# Revit family: REVIT-TPL-2017
name_source: partatom
category: Mechanical Equipment
revit_build: Autodesk Revit 2017 (Build: 20190507_1515(x64)
units: mm (PartAtom-declared; Revit-internal decimal feet)

## family parameters
Always vertical = No
Cut with Voids When Loaded = No
Part Type = Normal
Room Calculation Point = No
Round Connector Dimension = Use Radius
Shared = No
Work Plane-Based = No

## types (21) — shared parameters
Air Inlet Diameter = 6"
Air Inlet Extension = 18"
Air Inlet Radius = 3"
Apparent Load = 120 VA
Assembly Code = D3040400
Description = PVI Turbopower Low NOx- Water Heater
Disclaimer = This rendering is for building modeling purposes only. Submittal/catalog is still the contract document. PVI reserves the right to change design and specification without notice.
Drain Angle = 0.00°
Enclosure Location = 4"
Energy Radius = 14 1/2"
Flue Collector Radius = 11 1/4"
Flue Diameter = 8"
Flue Extension = 18 1/4"
Flue Radius = 4"
Gas Inlet Extension = 22"
Manufacturer = PVI Industries, LLC
NOx Extension = 18"
NOx Radius = 17"
Rear Access Extension = 0"
Relief Valve NPT = 1"
Relief Valve Radius = 1/2"
URL = www.pvi.com

## per-type parameters (varying)
- 1000 X 150A-TPL: Air Inlet Location=54 3/8"; Cold Water Extension=19 1/8"; Cold Water NPT=2"; Cold Water Radius=1"; Control Panel Extension=25 1/8"; Current=9 A; Drain Extension=21 1/8"; Drain NPT=1"; Drain Radius=1/2"; Energy Extension=37 1/8"; FC OAL=45 3/8"; Flat Side Distance=34"; Flue Collector Extension=8 1/4"; Flue Location=41 1/4"; Front Skid Extension=54 3/8"; Gas Inlet Height=32 1/2"; Gas Inlet NPT=1"; Gas Inlet Radius=1/2"; Height to Cold Inlet=17"; Height to Drain=1 7/8"; Height to Energy=26 1/2"; Height to Hot Outlet=44 7/8"; Height to Relief=51 7/8"; Hot Outlet Angle=0.00°; Hot Water Extension=19 1/8"; Hot Water NPT=2"; Hot Water Radius=1"; Input Btu/h=800000; Rear Skid Extension=18 1/8"; Recovery Rate 40F to 140F (gph)=800; Relief Extension=22 1/8"; Skid Center Dist=8 1/2"; Skid Length=36 1/4"; Skid Spacing=17"; Unit Height=63"; Unit Radius=18 1/8"; Weight=1325
- 1000 X 175A-TPL: Air Inlet Location=54 3/8"; Cold Water Extension=19 1/8"; Cold Water NPT=2"; Cold Water Radius=1"; Control Panel Extension=25 1/8"; Current=9 A; Drain Extension=21 1/8"; Drain NPT=1"; Drain Radius=1/2"; Energy Extension=37 1/8"; FC OAL=45 3/8"; Flat Side Distance=34"; Flue Collector Extension=8 1/4"; Flue Location=41 1/4"; Front Skid Extension=54 3/8"; Gas Inlet Height=32 1/2"; Gas Inlet NPT=1"; Gas Inlet Radius=1/2"; Height to Cold Inlet=17"; Height to Drain=1 7/8"; Height to Energy=26 1/2"; Height to Hot Outlet=50 7/8"; Height to Relief=57 7/8"; Hot Outlet Angle=0.00°; Hot Water Extension=19 1/8"; Hot Water NPT=2"; Hot Water Radius=1"; Input Btu/h=800000; Rear Skid Extension=18 1/8"; Recovery Rate 40F to 140F (gph)=800; Relief Extension=22 1/8"; Skid Center Dist=8 1/2"; Skid Length=36 1/4"; Skid Spacing=17"; Unit Height=69"; Unit Radius=18 1/8"; Weight=1380
- 1000 X 215A-TPL: Air Inlet Location=54 3/8"; Cold Water Extension=19 1/8"; Cold Water NPT=2"; Cold Water Radius=1"; Control Panel Extension=25 1/8"; Current=9 A; Drain Extension=21 1/8"; Drain NPT=1"; Drain Radius=1/2"; Energy Extension=37 1/8"; FC OAL=45 3/8"; Flat Side Distance=34"; Flue Collector Extension=8 1/4"; Flue Location=41 1/4"; Front Skid Extension=54 3/8"; Gas Inlet Height=32 1/2"; Gas Inlet NPT=1"; Gas Inlet Radius=1/2"; Height to Cold Inlet=17"; Height to Drain=1 7/8"; Height to Energy=26 1/2"; Height to Hot Outlet=64 1/4"; Height to Relief=64 7/8"; Hot Outlet Angle=90.00°; Hot Water Extension=19 1/8"; Hot Water NPT=2"; Hot Water Radius=1"; Input Btu/h=800000; Rear Skid Extension=18 1/8"; Recovery Rate 40F to 140F (gph)=800; Relief Extension=22 1/8"; Skid Center Dist=8 1/2"; Skid Length=36 1/4"; Skid Spacing=17"; Unit Height=76"; Unit Radius=18 1/8"; Weight=1430
- 1000 X 250A-TPL: Air Inlet Location=44 3/8"; Cold Water Extension=23 5/8"; Cold Water NPT=2"; Cold Water Radius=1"; Control Panel Extension=29 5/8"; Current=9 A; Drain Extension=25 5/8"; Drain NPT=1"; Drain Radius=1/2"; Energy Extension=27 1/8"; FC OAL=35 3/8"; Flat Side Distance=45 1/4"; Flue Collector Extension=8 1/4"; Flue Location=31 1/4"; Front Skid Extension=68 1/8"; Gas Inlet Height=32 1/2"; Gas Inlet NPT=1 1/4"; Gas Inlet Radius=5/8"; Height to Cold Inlet=17"; Height to Drain=1 7/8"; Height to Energy=28 3/4"; Height to Hot Outlet=38 7/8"; Height to Relief=45 1/8"; Hot Outlet Angle=0.00°; Hot Water Extension=23 5/8"; Hot Water NPT=2"; Hot Water Radius=1"; Input Btu/h=800000; Rear Skid Extension=22 5/8"; Recovery Rate 40F to 140F (gph)=800; Relief Extension=26 5/8"; Skid Center Dist=13 1/2"; Skid Length=45 1/2"; Skid Spacing=27"; Unit Height=61 1/2"; Unit Radius=22 5/8"; Weight=1380
- 1500 X 250A-TPL: Air Inlet Location=62 5/8"; Cold Water Extension=23 5/8"; Cold Water NPT=2"; Cold Water Radius=1"; Control Panel Extension=29 5/8"; Current=16 A; Drain Extension=25 5/8"; Drain NPT=1"; Drain Radius=1/2"; Energy Extension=38 1/8"; FC OAL=53 5/8"; Flat Side Distance=45 1/4"; Flue Collector Extension=15 1/2"; Flue Location=45 7/8"; Front Skid Extension=77 5/8"; Gas Inlet Height=32 1/2"; Gas Inlet NPT=2"; Gas Inlet Radius=1"; Height to Cold Inlet=17"; Height to Drain=1 7/8"; Height to Energy=28 3/4"; Height to Hot Outlet=38 7/8"; Height to Relief=45 1/8"; Hot Outlet Angle=0.00°; Hot Water Extension=23 5/8"; Hot Water NPT=2"; Hot Water Radius=1"; Input Btu/h=1200000; Rear Skid Extension=22 5/8"; Recovery Rate 40F to 140F (gph)=1200; Relief Extension=26 5/8"; Skid Center Dist=13 1/2"; Skid Length=55"; Skid Spacing=27"; Unit Height=61 1/2"; Unit Radius=22 5/8"; Weight=1750
- 1000 X 300A-TPL: Air Inlet Location=44 3/8"; Cold Water Extension=23 5/8"; Cold Water NPT=2"; Cold Water Radius=1"; Control Panel Extension=29 5/8"; Current=9 A; Drain Extension=25 5/8"; Drain NPT=1"; Drain Radius=1/2"; Energy Extension=27 1/8"; FC OAL=35 3/8"; Flat Side Distance=45 1/4"; Flue Collector Extension=8 1/4"; Flue Location=31 1/4"; Front Skid Extension=68 1/8"; Gas Inlet Height=32 1/2"; Gas Inlet NPT=1 1/4"; Gas Inlet Radius=5/8"; Height to Cold Inlet=17"; Height to Drain=1 7/8"; Height to Energy=28 3/4"; Height to Hot Outlet=50 7/8"; Height to Relief=57 1/8"; Hot Outlet Angle=0.00°; Hot Water Extension=23 5/8"; Hot Water NPT=2"; Hot Water Radius=1"; Input Btu/h=800000; Rear Skid Extension=22 5/8"; Recovery Rate 40F to 140F (gph)=800; Relief Extension=26 5/8"; Skid Center Dist=13 1/2"; Skid Length=45 1/2"; Skid Spacing=27"; Unit Height=73 1/2"; Unit Radius=22 5/8"; Weight=1445
- 1500 X 300A-TPL: Air Inlet Location=62 5/8"; Cold Water Extension=23 5/8"; Cold Water NPT=2"; Cold Water Radius=1"; Control Panel Extension=29 5/8"; Current=16 A; Drain Extension=25 5/8"; Drain NPT=1"; Drain Radius=1/2"; Energy Extension=38 1/8"; FC OAL=53 5/8"; Flat Side Distance=45 1/4"; Flue Collector Extension=15 1/2"; Flue Location=45 7/8"; Front Skid Extension=77 5/8"; Gas Inlet Height=32 1/2"; Gas Inlet NPT=2"; Gas Inlet Radius=1"; Height to Cold Inlet=17"; Height to Drain=1 7/8"; Height to Energy=28 3/4"; Height to Hot Outlet=50 7/8"; Height to Relief=57 1/8"; Hot Outlet Angle=0.00°; Hot Water Extension=23 5/8"; Hot Water NPT=2"; Hot Water Radius=1"; Input Btu/h=1200000; Rear Skid Extension=22 5/8"; Recovery Rate 40F to 140F (gph)=1200; Relief Extension=26 5/8"; Skid Center Dist=13 1/2"; Skid Length=55"; Skid Spacing=27"; Unit Height=73 1/2"; Unit Radius=22 5/8"; Weight=1840
- 1000 X 400A-TPL: Air Inlet Location=44 3/8"; Cold Water Extension=23 5/8"; Cold Water NPT=2"; Cold Water Radius=1"; Control Panel Extension=29 5/8"; Current=9 A; Drain Extension=25 5/8"; Drain NPT=1"; Drain Radius=1/2"; Energy Extension=27 1/8"; FC OAL=35 3/8"; Flat Side Distance=45 1/4"; Flue Collector Extension=8 1/4"; Flue Location=31 1/4"; Front Skid Extension=68 1/8"; Gas Inlet Height=32 1/2"; Gas Inlet NPT=1"; Gas Inlet Radius=1/2"; Height to Cold Inlet=17"; Height to Drain=1 7/8"; Height to Energy=28 3/4"; Height to Hot Outlet=68 1/2"; Height to Relief=69 1/8"; Hot Outlet Angle=90.00°; Hot Water Extension=23 5/8"; Hot Water NPT=2"; Hot Water Radius=1"; Input Btu/h=800000; Rear Skid Extension=22 5/8"; Recovery Rate 40F to 140F (gph)=800; Relief Extension=26 5/8"; Skid Center Dist=13 1/2"; Skid Length=45 1/2"; Skid Spacing=27"; Unit Height=85 1/2"; Unit Radius=22 5/8"; Weight=1575
- 1500 X 400A-TPL: Air Inlet Location=62 5/8"; Cold Water Extension=23 5/8"; Cold Water NPT=2"; Cold Water Radius=1"; Control Panel Extension=29 5/8"; Current=16 A; Drain Extension=25 5/8"; Drain NPT=1"; Drain Radius=1/2"; Energy Extension=38 1/8"; FC OAL=53 5/8"; Flat Side Distance=45 1/4"; Flue Collector Extension=15 1/2"; Flue Location=45 7/8"; Front Skid Extension=77 5/8"; Gas Inlet Height=32 1/2"; Gas Inlet NPT=1 1/4"; Gas Inlet Radius=5/8"; Height to Cold Inlet=17"; Height to Drain=1 7/8"; Height to Energy=28 3/4"; Height to Hot Outlet=68 1/2"; Height to Relief=69 1/8"; Hot Outlet Angle=90.00°; Hot Water Extension=23 5/8"; Hot Water NPT=2"; Hot Water Radius=1"; Input Btu/h=1200000; Rear Skid Extension=22 5/8"; Recovery Rate 40F to 140F (gph)=1200; Relief Extension=26 5/8"; Skid Center Dist=13 1/2"; Skid Length=55"; Skid Spacing=27"; Unit Height=85 1/2"; Unit Radius=22 5/8"; Weight=1925
- 1000 X 500 A-TPL: Air Inlet Location=49 7/8"; Cold Water Extension=28 7/8"; Cold Water NPT=3"; Cold Water Radius=1 1/2"; Control Panel Extension=34 7/8"; Current=9 A; Drain Extension=30 7/8"; Drain NPT=1 1/2"; Drain Radius=3/4"; Energy Extension=32 5/8"; FC OAL=40 7/8"; Flat Side Distance=55 3/4"; Flue Collector Extension=8 1/4"; Flue Location=36 3/4"; Front Skid Extension=82 7/8"; Gas Inlet Height=33 1/2"; Gas Inlet NPT=1"; Gas Inlet Radius=1/2"; Height to Cold Inlet=18 1/4"; Height to Drain=2 1/4"; Height to Energy=30"; Height to Hot Outlet=57 3/8"; Height to Relief=58"; Hot Outlet Angle=90.00°; Hot Water Extension=28 7/8"; Hot Water NPT=3"; Hot Water Radius=1 1/2"; Input Btu/h=800000; Rear Skid Extension=27 7/8"; Recovery Rate 40F to 140F (gph)=800; Relief Extension=31 7/8"; Skid Center Dist=13 1/2"; Skid Length=55"; Skid Spacing=27"; Unit Height=75 3/4"; Unit Radius=27 7/8"; Weight=2100
- 1000 X 600 A-TPL: Air Inlet Location=49 7/8"; Cold Water Extension=28 7/8"; Cold Water NPT=3"; Cold Water Radius=1 1/2"; Control Panel Extension=34 7/8"; Current=9 A; Drain Extension=30 7/8"; Drain NPT=1 1/2"; Drain Radius=3/4"; Energy Extension=32 5/8"; FC OAL=40 7/8"; Flat Side Distance=55 3/4"; Flue Collector Extension=8 1/4"; Flue Location=36 3/4"; Front Skid Extension=82 7/8"; Gas Inlet Height=33 1/2"; Gas Inlet NPT=1"; Gas Inlet Radius=1/2"; Height to Cold Inlet=18 1/4"; Height to Drain=2 1/4"; Height to Energy=30"; Height to Hot Outlet=69 3/8"; Height to Relief=70"; Hot Outlet Angle=90.00°; Hot Water Extension=28 7/8"; Hot Water NPT=3"; Hot Water Radius=1 1/2"; Input Btu/h=800000; Rear Skid Extension=27 7/8"; Recovery Rate 40F to 140F (gph)=800; Relief Extension=31 7/8"; Skid Center Dist=13 1/2"; Skid Length=55"; Skid Spacing=27"; Unit Height=87 3/4"; Unit Radius=27 7/8"; Weight=2180
- 1500 X 500 A-TPL: Air Inlet Location=57 7/8"; Cold Water Extension=28 7/8"; Cold Water NPT=3"; Cold Water Radius=1 1/2"; Control Panel Extension=34 7/8"; Current=16 A; Drain Extension=30 7/8"; Drain NPT=1 1/2"; Drain Radius=3/4"; Energy Extension=33 3/8"; FC OAL=48 7/8"; Flat Side Distance=55 3/4"; Flue Collector Extension=15 1/2"; Flue Location=41 1/8"; Front Skid Extension=82 7/8"; Gas Inlet Height=33 1/2"; Gas Inlet NPT=1 1/4"; Gas Inlet Radius=5/8"; Height to Cold Inlet=18 1/4"; Height to Drain=2 1/4"; Height to Energy=30"; Height to Hot Outlet=57 3/8"; Height to Relief=70"; Hot Outlet Angle=90.00°; Hot Water Extension=28 7/8"; Hot Water NPT=3"; Hot Water Radius=1 1/2"; Input Btu/h=1200000; Rear Skid Extension=27 7/8"; Recovery Rate 40F to 140F (gph)=1200; Relief Extension=31 7/8"; Skid Center Dist=13 1/2"; Skid Length=55"; Skid Spacing=27"; Unit Height=75 3/4"; Unit Radius=27 7/8"; Weight=2370
- 1500 X 600 A-TPL: Air Inlet Location=57 7/8"; Cold Water Extension=28 7/8"; Cold Water NPT=3"; Cold Water Radius=1 1/2"; Control Panel Extension=34 7/8"; Current=16 A; Drain Extension=30 7/8"; Drain NPT=1 1/2"; Drain Radius=3/4"; Energy Extension=33 3/8"; FC OAL=48 7/8"; Flat Side Distance=55 3/4"; Flue Collector Extension=15 1/2"; Flue Location=41 1/8"; Front Skid Extension=82 7/8"; Gas Inlet Height=33 1/2"; Gas Inlet NPT=1 1/4"; Gas Inlet Radius=5/8"; Height to Cold Inlet=18 1/4"; Height to Drain=2 1/4"; Height to Energy=30"; Height to Hot Outlet=69 3/8"; Height to Relief=58"; Hot Outlet Angle=90.00°; Hot Water Extension=28 7/8"; Hot Water NPT=3"; Hot Water Radius=1 1/2"; Input Btu/h=1200000; Rear Skid Extension=27 7/8"; Recovery Rate 40F to 140F (gph)=1200; Relief Extension=31 7/8"; Skid Center Dist=13 1/2"; Skid Length=55"; Skid Spacing=27"; Unit Height=87 3/4"; Unit Radius=27 7/8"; Weight=2445
- 1000 X 750 A-TPL: Air Inlet Location=55 1/2"; Cold Water Extension=34 1/4"; Cold Water NPT=3"; Cold Water Radius=1 1/2"; Control Panel Extension=40 1/4"; Current=9 A; Drain Extension=36 1/4"; Drain NPT=1 1/2"; Drain Radius=3/4"; Energy Extension=38 1/4"; FC OAL=46 1/2"; Flat Side Distance=66 1/2"; Flue Collector Extension=8 1/4"; Flue Location=42 3/8"; Front Skid Extension=100 1/4"; Gas Inlet Height=36 1/2"; Gas Inlet NPT=1"; Gas Inlet Radius=1/2"; Height to Cold Inlet=21 1/4"; Height to Drain=2 1/4"; Height to Energy=32 5/8"; Height to Hot Outlet=60 7/8"; Height to Relief=61 1/2"; Hot Outlet Angle=90.00°; Hot Water Extension=34 1/4"; Hot Water NPT=3"; Hot Water Radius=1 1/2"; Input Btu/h=800000; Rear Skid Extension=33 1/4"; Recovery Rate 40F to 140F (gph)=800; Relief Extension=37 1/4"; Skid Center Dist=18"; Skid Length=67"; Skid Spacing=36"; Unit Height=81 1/4"; Unit Radius=33 1/4"; Weight=2280
- 1500 X 750 A-TPL: Air Inlet Location=63 1/2"; Cold Water Extension=34 1/4"; Cold Water NPT=3"; Cold Water Radius=1 1/2"; Control Panel Extension=40 1/4"; Current=16 A; Drain Extension=36 1/4"; Drain NPT=1 1/2"; Drain Radius=3/4"; Energy Extension=39"; FC OAL=54 1/2"; Flat Side Distance=66 1/2"; Flue Collector Extension=15 1/2"; Flue Location=46 3/4"; Front Skid Extension=100 1/4"; Gas Inlet Height=36 1/2"; Gas Inlet NPT=1 1/4"; Gas Inlet Radius=5/8"; Height to Cold Inlet=21 1/4"; Height to Drain=2 1/4"; Height to Energy=32 5/8"; Height to Hot Outlet=60 7/8"; Height to Relief=61 1/2"; Hot Outlet Angle=90.00°; Hot Water Extension=34 1/4"; Hot Water NPT=3"; Hot Water Radius=1 1/2"; Input Btu/h=1200000; Rear Skid Extension=33 1/4"; Recovery Rate 40F to 140F (gph)=1200; Relief Extension=37 1/4"; Skid Center Dist=18"; Skid Length=67"; Skid Spacing=36"; Unit Height=81 1/4"; Unit Radius=33 1/4"; Weight=2320
- 1000 X 900 A-TPL: Air Inlet Location=55 1/2"; Cold Water Extension=34 1/4"; Cold Water NPT=3"; Cold Water Radius=1 1/2"; Control Panel Extension=40 1/4"; Current=9 A; Drain Extension=36 1/4"; Drain NPT=1 1/2"; Drain Radius=3/4"; Energy Extension=38 1/4"; FC OAL=46 1/2"; Flat Side Distance=66 1/2"; Flue Collector Extension=8 1/4"; Flue Location=42 3/8"; Front Skid Extension=100 1/4"; Gas Inlet Height=36 1/2"; Gas Inlet NPT=1"; Gas Inlet Radius=1/2"; Height to Cold Inlet=21 1/4"; Height to Drain=2 1/4"; Height to Energy=32 5/8"; Height to Hot Outlet=72 7/8"; Height to Relief=73 1/2"; Hot Outlet Angle=90.00°; Hot Water Extension=34 1/4"; Hot Water NPT=3"; Hot Water Radius=1 1/2"; Input Btu/h=800000; Rear Skid Extension=33 1/4"; Recovery Rate 40F to 140F (gph)=800; Relief Extension=37 1/4"; Skid Center Dist=18"; Skid Length=67"; Skid Spacing=36"; Unit Height=93 1/4"; Unit Radius=33 1/4"; Weight=2550
- 1500 X 900 A-TPL: Air Inlet Location=63 1/2"; Cold Water Extension=34 1/4"; Cold Water NPT=3"; Cold Water Radius=1 1/2"; Control Panel Extension=40 1/4"; Current=16 A; Drain Extension=36 1/4"; Drain NPT=1 1/2"; Drain Radius=3/4"; Energy Extension=39"; FC OAL=54 1/2"; Flat Side Distance=66 1/2"; Flue Collector Extension=15 1/2"; Flue Location=46 3/4"; Front Skid Extension=100 1/4"; Gas Inlet Height=36 1/2"; Gas Inlet NPT=1 1/4"; Gas Inlet Radius=5/8"; Height to Cold Inlet=21 1/4"; Height to Drain=2 1/4"; Height to Energy=32 5/8"; Height to Hot Outlet=72 7/8"; Height to Relief=73 1/2"; Hot Outlet Angle=90.00°; Hot Water Extension=34 1/4"; Hot Water NPT=3"; Hot Water Radius=1 1/2"; Input Btu/h=1200000; Rear Skid Extension=33 1/4"; Recovery Rate 40F to 140F (gph)=1200; Relief Extension=37 1/4"; Skid Center Dist=18"; Skid Length=67"; Skid Spacing=36"; Unit Height=93 1/4"; Unit Radius=33 1/4"; Weight=3000
- 1000 X 1250 A-TPL: Air Inlet Location=61"; Cold Water Extension=38 1/2"; Cold Water NPT=3"; Cold Water Radius=1 1/2"; Control Panel Extension=44 1/2"; Current=9 A; Drain Extension=40 1/2"; Drain NPT=1 1/2"; Drain Radius=3/4"; Energy Extension=43 3/4"; FC OAL=52"; Flat Side Distance=75"; Flue Collector Extension=8 1/4"; Flue Location=47 7/8"; Front Skid Extension=112 1/2"; Gas Inlet Height=35 1/2"; Gas Inlet NPT=1"; Gas Inlet Radius=1/2"; Height to Cold Inlet=21 1/4"; Height to Drain=2 1/4"; Height to Energy=32 3/8"; Height to Hot Outlet=72 1/2"; Height to Relief=73 1/8"; Hot Outlet Angle=90.00°; Hot Water Extension=38 1/2"; Hot Water NPT=3"; Hot Water Radius=1 1/2"; Input Btu/h=800000; Rear Skid Extension=37 1/2"; Recovery Rate 40F to 140F (gph)=800; Relief Extension=41 1/2"; Skid Center Dist=21 1/2"; Skid Length=75"; Skid Spacing=43"; Unit Height=92 1/2"; Unit Radius=37 1/2"; Weight=3860
- 1500 X 1250 A-TPL: Air Inlet Location=69"; Cold Water Extension=38 1/2"; Cold Water NPT=3"; Cold Water Radius=1 1/2"; Control Panel Extension=44 1/2"; Current=16 A; Drain Extension=40 1/2"; Drain NPT=1 1/2"; Drain Radius=3/4"; Energy Extension=44 1/2"; FC OAL=60"; Flat Side Distance=75"; Flue Collector Extension=15 1/2"; Flue Location=52 1/4"; Front Skid Extension=112 1/2"; Gas Inlet Height=35 1/2"; Gas Inlet NPT=1 1/4"; Gas Inlet Radius=5/8"; Height to Cold Inlet=21 1/4"; Height to Drain=2 1/4"; Height to Energy=32 3/8"; Height to Hot Outlet=72 1/2"; Height to Relief=73 1/8"; Hot Outlet Angle=90.00°; Hot Water Extension=38 1/2"; Hot Water NPT=3"; Hot Water Radius=1 1/2"; Input Btu/h=1200000; Rear Skid Extension=37 1/2"; Recovery Rate 40F to 140F (gph)=1200; Relief Extension=41 1/2"; Skid Center Dist=21 1/2"; Skid Length=75"; Skid Spacing=43"; Unit Height=92 1/2"; Unit Radius=37 1/2"; Weight=3870
- 1000 X 1500 A-TPL: Air Inlet Location=61"; Cold Water Extension=38 1/2"; Cold Water NPT=3"; Cold Water Radius=1 1/2"; Control Panel Extension=44 1/2"; Current=9 A; Drain Extension=40 1/2"; Drain NPT=1 1/2"; Drain Radius=3/4"; Energy Extension=43 3/4"; FC OAL=52"; Flat Side Distance=75"; Flue Collector Extension=8 1/4"; Flue Location=47 7/8"; Front Skid Extension=112 1/2"; Gas Inlet Height=35 1/2"; Gas Inlet NPT=1"; Gas Inlet Radius=1/2"; Height to Cold Inlet=21 1/4"; Height to Drain=2 1/4"; Height to Energy=32 3/8"; Height to Hot Outlet=84 1/2"; Height to Relief=85 1/8"; Hot Outlet Angle=90.00°; Hot Water Extension=38 1/2"; Hot Water NPT=3"; Hot Water Radius=1 1/2"; Input Btu/h=800000; Rear Skid Extension=37 1/2"; Recovery Rate 40F to 140F (gph)=800; Relief Extension=41 1/2"; Skid Center Dist=21 1/2"; Skid Length=75"; Skid Spacing=43"; Unit Height=104 1/2"; Unit Radius=37 1/2"; Weight=4075
- 1500 X 1500 A-TPL: Air Inlet Location=69"; Cold Water Extension=38 1/2"; Cold Water NPT=3"; Cold Water Radius=1 1/2"; Control Panel Extension=44 1/2"; Current=16 A; Drain Extension=40 1/2"; Drain NPT=1 1/2"; Drain Radius=3/4"; Energy Extension=44 1/2"; FC OAL=60"; Flat Side Distance=75"; Flue Collector Extension=15 1/2"; Flue Location=52 1/4"; Front Skid Extension=112 1/2"; Gas Inlet Height=35 1/2"; Gas Inlet NPT=1 1/4"; Gas Inlet Radius=5/8"; Height to Cold Inlet=21 1/4"; Height to Drain=2 1/4"; Height to Energy=32 3/8"; Height to Hot Outlet=84 1/2"; Height to Relief=85 1/8"; Hot Outlet Angle=90.00°; Hot Water Extension=38 1/2"; Hot Water NPT=3"; Hot Water Radius=1 1/2"; Input Btu/h=1200000; Rear Skid Extension=37 1/2"; Recovery Rate 40F to 140F (gph)=1200; Relief Extension=41 1/2"; Skid Center Dist=21 1/2"; Skid Length=75"; Skid Spacing=43"; Unit Height=104 1/2"; Unit Radius=37 1/2"; Weight=4085

note: column(s) folded — value = type name in every type: Model

## geometry (parser evidence)
native form markers: Blend x2, Sweep x3
no freeform markers — native parametric forms only
